annotation { "Feature Type Name" : "Feature", "Feature Type Description" : "" }
export const myFeature = defineFeature(function(context is Context, id is Id, definition is map)
    precondition{}
    {
        {
            var Q0;
            Q0=qCreatedBy(makeId("Top.planeOp"),FACE);
            var sketch = newSketch(context, id + "F0", { "sketchPlane" : qUnion([Q0])});
            skLineSegment(sketch, "E0.bottom", {"start": v(-19.05, 12.7) * mm, "end": v(19.05, 12.7) * mm});
            skLineSegment(sketch, "E0.top", {"start": v(-25.4, -25.4) * mm, "end": v(25.4, -25.4) * mm});
            skLineSegment(sketch, "E0.left", {"start": v(-25.4, 6.35) * mm, "end": v(-25.4, -25.4) * mm});
            skLineSegment(sketch, "E0.right", {"start": v(25.4, 6.35) * mm, "end": v(25.4, -25.4) * mm});
            skLineSegment(sketch, "E1.0", {"start": v(-17.78, 11.43) * mm, "end": v(17.78, 11.43) * mm});
            skLineSegment(sketch, "E1.1", {"start": v(-24.13, 5.08) * mm, "end": v(-24.13, -22.86) * mm});
            skLineSegment(sketch, "E1.2", {"start": v(-22.86, -24.13) * mm, "end": v(22.86, -24.13) * mm});
            skLineSegment(sketch, "E1.3", {"start": v(24.13, 5.08) * mm, "end": v(24.13, -22.86) * mm});
            skLineSegment(sketch, "E2.top", {"start": v(-25.4, -38.1) * mm, "end": v(25.4, -38.1) * mm});
            skLineSegment(sketch, "E2.left", {"start": v(-25.4, -27.94) * mm, "end": v(-25.4, -38.1) * mm});
            skLineSegment(sketch, "E2.right", {"start": v(25.4, -27.94) * mm, "end": v(25.4, -38.1) * mm});
            skLineSegment(sketch, "E3", {"start": v(-25.4, -27.94) * mm, "end": v(25.4, -27.94) * mm});
            skPoint(sketch, "E3.endSnap0", {"position": v(25.4, -31.75) * mm});
            skLineSegment(sketch, "E4", {"start": v(-20.32, -25.4) * mm, "end": v(-20.32, -27.94) * mm});
            skLineSegment(sketch, "E5", {"start": v(20.32, -25.4) * mm, "end": v(20.32, -27.94) * mm});
            skPoint(sketch, "E6.visualSharp", {"position": v(-24.13, 11.43) * mm});
            skArc(sketch, "E6.filletArc", {"start": v(-17.78, 11.43) * mm, "mid": v(-22.27, 9.57) * mm, "end": v(-24.13, 5.08) * mm});
            skPoint(sketch, "E7.visualSharp", {"position": v(-25.4, 12.7) * mm});
            skArc(sketch, "E7.filletArc", {"start": v(-19.05, 12.7) * mm, "mid": v(-23.54, 10.84) * mm, "end": v(-25.4, 6.35) * mm});
            skPoint(sketch, "E8.visualSharp", {"position": v(24.13, 11.43) * mm});
            skArc(sketch, "E8.filletArc", {"start": v(24.13, 5.08) * mm, "mid": v(22.27, 9.57) * mm, "end": v(17.78, 11.43) * mm});
            skPoint(sketch, "E9.visualSharp", {"position": v(25.4, 12.7) * mm});
            skArc(sketch, "E9.filletArc", {"start": v(25.4, 6.35) * mm, "mid": v(23.54, 10.84) * mm, "end": v(19.05, 12.7) * mm});
            skArc(sketch, "E10.filletArc", {"start": v(-24.13, -22.86) * mm, "mid": v(-23.76, -23.76) * mm, "end": v(-22.86, -24.13) * mm});
            skArc(sketch, "E11.filletArc", {"start": v(22.86, -24.13) * mm, "mid": v(23.76, -23.76) * mm, "end": v(24.13, -22.86) * mm});
            skSolve(sketch);
        }
        {
            var Q0;
            Q0=makeQuery(id+"F0.imprint","IMPRINT",FACE,{"disambiguationData":[TD([[makeQuery(id+"F0.imprint","IMPRINT",EDGE,{"derivedFrom":sQuery(id+"F0.wireOp",EDGE,"E0.bottom")}),-1.0]])]});
            extrude(context, id + "F1", {"entities" : qUnion([Q0]), "depth" : 50.8 * mm});
        }
        {
            var Q0;
            Q0=makeQuery(id+"F0.imprint","IMPRINT",FACE,{"disambiguationData":[TD([[makeQuery(id+"F0.imprint","IMPRINT",EDGE,{"derivedFrom":sQuery(id+"F0.wireOp",EDGE,"E1.0")}),-1.0]])]});
            var Q1;
            {var subQ0=sQuery(id+"F0.wireOp",EDGE,"E4");Q1=makeQuery(id+"F0.imprint","IMPRINT",FACE,{"disambiguationData":[TD([[makeQuery(id+"F0.imprint","IMPRINT",EDGE,{"derivedFrom":subQ0}),1.0]])]});}
            extrude(context, id + "F2", {"entities" : qUnion([Q0, Q1]), "operationType" : NewBodyOperationType.ADD, "depth" : 0.5 * mm});
        }
        {
            var Q0;
            Q0=makeQuery(id+"F0.imprint","IMPRINT",FACE,{"disambiguationData":[TD([[makeQuery(id+"F0.imprint","IMPRINT",EDGE,{"derivedFrom":sQuery(id+"F0.wireOp",EDGE,"E2.top")}),1.0]])]});
            extrude(context, id + "F3", {"entities" : qUnion([Q0]), "operationType" : NewBodyOperationType.ADD, "depth" : 7.62 * mm});
        }
        {
            var Q0;
            Q0=makeQuery(id+"F3.opExtrude","CAP_EDGE",EDGE,{"disambiguationData":[OSD([sQuery(id+"F0.wireOp",EDGE,"E2.top")])],"isStart":false});
            chamfer(context, id + "F4", {"entities" : qUnion([Q0]), "chamferType" : ChamferType.TWO_OFFSETS, "width1" : 8.9 * mm, "oppositeDirection" : false, "width2" : 3.8 * mm, "tangentPropagation" : true});
        }
        {
            var Q0;
            Q0=makeQuery(id+"F4.opChamfer","BLEND_FACE",FACE,{"disambiguationData":[OSD([sQuery(id+"F0.wireOp",EDGE,"E2.top")])]});
            var Q1;
            Q1=makeQuery(id+"F3.opExtrude","SWEPT_EDGE",EDGE,{"disambiguationData":[OSD([sQuery(id+"F0.wireOp",EDGE,"E2.left"),sQuery(id+"F0.wireOp",EDGE,"E3")])]});
            var Q2;
            Q2=makeQuery(id+"F3.opExtrude","SWEPT_EDGE",EDGE,{"disambiguationData":[OSD([sQuery(id+"F0.wireOp",EDGE,"E2.top"),sQuery(id+"F0.wireOp",EDGE,"E2.left")])]});
            var Q3;
            Q3=makeQuery(id+"F3.opExtrude","SWEPT_EDGE",EDGE,{"disambiguationData":[OSD([sQuery(id+"F0.wireOp",EDGE,"E2.top"),sQuery(id+"F0.wireOp",EDGE,"E2.right")])]});
            var Q4;
            Q4=makeQuery(id+"F3.opExtrude","SWEPT_EDGE",EDGE,{"disambiguationData":[OSD([sQuery(id+"F0.wireOp",EDGE,"E2.right"),sQuery(id+"F0.wireOp",EDGE,"E3")])]});
            fillet(context, id + "F5", {"entities" : qUnion([Q0, Q1, Q2, Q3, Q4]), "radius" : 1.27 * mm, "tangentPropagation" : true, "allowEdgeOverflow" : false});
        }
        {
            var Q0;
            Q0=makeQuery(id+"F1.opExtrude","SWEPT_FACE",FACE,{"disambiguationData":[OSD([sQuery(id+"F0.wireOp",EDGE,"E0.top")])]});
            var sketch = newSketch(context, id + "F6", { "sketchPlane" : qUnion([Q0])});
            skLineSegment(sketch, "E12.bottom", {"start": v(-15.24, 47) * mm, "end": v(15.24, 47) * mm});
            skLineSegment(sketch, "E12.top", {"start": v(-15.24, 11.43) * mm, "end": v(15.24, 11.43) * mm});
            skLineSegment(sketch, "E12.left", {"start": v(-21.59, 40.64) * mm, "end": v(-21.59, 17.78) * mm});
            skLineSegment(sketch, "E12.right", {"start": v(21.6, 40.64) * mm, "end": v(21.6, 17.78) * mm});
            skPoint(sketch, "E13.visualSharp", {"position": v(-21.59, 47) * mm});
            skArc(sketch, "E13.filletArc", {"start": v(-15.24, 47) * mm, "mid": v(-19.73, 45.13) * mm, "end": v(-21.59, 40.64) * mm});
            skPoint(sketch, "E14.visualSharp", {"position": v(-21.6, 11.43) * mm});
            skArc(sketch, "E14.filletArc", {"start": v(-21.59, 17.78) * mm, "mid": v(-19.73, 13.29) * mm, "end": v(-15.24, 11.43) * mm});
            skPoint(sketch, "E15.visualSharp", {"position": v(21.6, 11.43) * mm});
            skArc(sketch, "E15.filletArc", {"start": v(15.24, 11.43) * mm, "mid": v(19.73, 13.29) * mm, "end": v(21.6, 17.78) * mm});
            skPoint(sketch, "E16.visualSharp", {"position": v(21.6, 47) * mm});
            skArc(sketch, "E16.filletArc", {"start": v(21.6, 40.64) * mm, "mid": v(19.73, 45.13) * mm, "end": v(15.24, 46.99) * mm});
            skSolve(sketch);
        }
        {
            var Q0;
            Q0=makeQuery(id+"F6.imprint","IMPRINT",FACE,{"disambiguationData":[TD([[makeQuery(id+"F6.imprint","IMPRINT",EDGE,{"derivedFrom":sQuery(id+"F6.wireOp",EDGE,"E12.bottom")}),-1.0]])]});
            extrude(context, id + "F7", {"entities" : qUnion([Q0]), "operationType" : NewBodyOperationType.REMOVE, "oppositeDirection" : true, "depth" : 0.38 * mm});
        }
        {
            var Q0;
            Q0=makeQuery(id+"F7.boolean.opBoolean","COPY",FACE,{"derivedFrom":makeQuery(id+"F7.opExtrude","CAP_FACE",FACE,{"disambiguationData":[OSD([sQuery(id+"F6.wireOp",EDGE,"E12.bottom"),sQuery(id+"F6.wireOp",EDGE,"E12.top"),sQuery(id+"F6.wireOp",EDGE,"E12.left"),sQuery(id+"F6.wireOp",EDGE,"E12.right"),sQuery(id+"F6.wireOp",EDGE,"E13.filletArc"),sQuery(id+"F6.wireOp",EDGE,"E14.filletArc"),sQuery(id+"F6.wireOp",EDGE,"E15.filletArc"),sQuery(id+"F6.wireOp",EDGE,"E16.filletArc")])],"isStart":false})});
            var sketch = newSketch(context, id + "F8", { "sketchPlane" : qUnion([Q0])});
            skText(sketch, "E17", { "text": "DA DA", "fontName": "OpenSans-Regular.ttf"});
            skPoint(sketch, "E17.firstSnap0", {"position": v(-19.73, 45.13) * mm});
            const initialGuessF8  = {"E17": [-0.01973, 0.02564, 1, 0, 0.0093]};
            skSetInitialGuess(sketch, initialGuessF8);
            skSolve(sketch);
        }
        {
            var Q0;
            Q0 = qSketchRegion(id + "F8", true);
            extrude(context, id + "F9", {"entities" : qUnion([Q0]), "operationType" : NewBodyOperationType.ADD, "depth" : 0.38 * mm});
        }
        {
            var Q0;
            Q0=makeQuery(id+"F1.opExtrude","SWEPT_FACE",FACE,{"disambiguationData":[OSD([sQuery(id+"F0.wireOp",EDGE,"E0.right")])]});
            var sketch = newSketch(context, id + "F10", { "sketchPlane" : qUnion([Q0])});
            skLineSegment(sketch, "E18.bottom", {"start": v(-25.4, 31.75) * mm, "end": v(6.35, 31.75) * mm});
            skLineSegment(sketch, "E18.top", {"start": v(-25.4, 25.4) * mm, "end": v(6.35, 25.4) * mm});
            skLineSegment(sketch, "E18.left", {"start": v(-25.4, 31.75) * mm, "end": v(-25.4, 25.4) * mm});
            skLineSegment(sketch, "E18.right", {"start": v(6.35, 31.75) * mm, "end": v(6.35, 25.4) * mm});
            skSolve(sketch);
        }
        {
            var Q0;
            Q0=makeQuery(id+"F10.imprint","IMPRINT",FACE,{"disambiguationData":[TD([[makeQuery(id+"F10.imprint","IMPRINT",EDGE,{"derivedFrom":sQuery(id+"F10.wireOp",EDGE,"E18.bottom")}),-1.0]])]});
            extrude(context, id + "F11", {"entities" : qUnion([Q0]), "operationType" : NewBodyOperationType.REMOVE, "oppositeDirection" : true, "depth" : 0.25 * mm});
        }
        {
            var Q0;
            Q0=makeQuery(id+"F1.opExtrude","SWEPT_FACE",FACE,{"disambiguationData":[OSD([sQuery(id+"F0.wireOp",EDGE,"E0.left")])]});
            var sketch = newSketch(context, id + "F12", { "sketchPlane" : qUnion([Q0])});
            skLineSegment(sketch, "E19.bottom", {"start": v(25.4, 31.75) * mm, "end": v(-6.35, 31.75) * mm});
            skLineSegment(sketch, "E19.top", {"start": v(25.4, 25.4) * mm, "end": v(-6.35, 25.4) * mm});
            skLineSegment(sketch, "E19.left", {"start": v(25.4, 31.75) * mm, "end": v(25.4, 25.4) * mm});
            skLineSegment(sketch, "E19.right", {"start": v(-6.35, 31.75) * mm, "end": v(-6.35, 25.4) * mm});
            skSolve(sketch);
        }
        {
            var Q0;
            Q0=makeQuery(id+"F12.imprint","IMPRINT",FACE,{"disambiguationData":[TD([[makeQuery(id+"F12.imprint","IMPRINT",EDGE,{"derivedFrom":sQuery(id+"F12.wireOp",EDGE,"E19.bottom")}),1.0]])]});
            extrude(context, id + "F13", {"entities" : qUnion([Q0]), "operationType" : NewBodyOperationType.REMOVE, "oppositeDirection" : true, "depth" : 0.25 * mm});
        }
        {
            var Q0;
            Q0=makeQuery(id+"F9.opExtrude","CAP_EDGE",EDGE,{"disambiguationData":[OSD([sQuery(id+"F8.wireOp",EDGE,"E17.sketch_text.stroke-2")])],"isStart":true});
            var Q1;
            Q1=makeQuery(id+"F9.opExtrude","CAP_EDGE",EDGE,{"disambiguationData":[OSD([sQuery(id+"F8.wireOp",EDGE,"E17.sketch_text.stroke-17")])],"isStart":true});
            var Q2;
            Q2=makeQuery(id+"F9.opExtrude","CAP_EDGE",EDGE,{"disambiguationData":[OSD([sQuery(id+"F8.wireOp",EDGE,"E17.sketch_text.stroke-18")])],"isStart":true});
            var Q3;
            Q3=makeQuery(id+"F9.opExtrude","CAP_EDGE",EDGE,{"disambiguationData":[OSD([sQuery(id+"F8.wireOp",EDGE,"E17.sketch_text.stroke-15")])],"isStart":true});
            var Q4;
            Q4=makeQuery(id+"F9.opExtrude","CAP_EDGE",EDGE,{"disambiguationData":[OSD([sQuery(id+"F8.wireOp",EDGE,"E17.sketch_text.stroke-21")])],"isStart":true});
            var Q5;
            Q5=makeQuery(id+"F9.boolean.opBoolean","SPLIT",FACE,{"disambiguationData":[TD([makeQuery(id+"F9.opExtrude","SWEPT_FACE",FACE,{"disambiguationData":[OSD([sQuery(id+"F8.wireOp",EDGE,"E17.sketch_text.stroke-49")])]})])],"derivedFrom":makeQuery(id+"F7.boolean.opBoolean","COPY",FACE,{"derivedFrom":makeQuery(id+"F7.opExtrude","CAP_FACE",FACE,{"disambiguationData":[OSD([sQuery(id+"F6.wireOp",EDGE,"E12.bottom"),sQuery(id+"F6.wireOp",EDGE,"E12.top"),sQuery(id+"F6.wireOp",EDGE,"E12.left"),sQuery(id+"F6.wireOp",EDGE,"E12.right"),sQuery(id+"F6.wireOp",EDGE,"E13.filletArc"),sQuery(id+"F6.wireOp",EDGE,"E14.filletArc"),sQuery(id+"F6.wireOp",EDGE,"E15.filletArc"),sQuery(id+"F6.wireOp",EDGE,"E16.filletArc")])],"isStart":false})})});
            var Q6;
            Q6=makeQuery(id+"F9.boolean.opBoolean","SPLIT",FACE,{"disambiguationData":[TD([makeQuery(id+"F9.opExtrude","SWEPT_FACE",FACE,{"disambiguationData":[OSD([sQuery(id+"F8.wireOp",EDGE,"E17.sketch_text.stroke-34")])]})])],"derivedFrom":makeQuery(id+"F7.boolean.opBoolean","COPY",FACE,{"derivedFrom":makeQuery(id+"F7.opExtrude","CAP_FACE",FACE,{"disambiguationData":[OSD([sQuery(id+"F6.wireOp",EDGE,"E12.bottom"),sQuery(id+"F6.wireOp",EDGE,"E12.top"),sQuery(id+"F6.wireOp",EDGE,"E12.left"),sQuery(id+"F6.wireOp",EDGE,"E12.right"),sQuery(id+"F6.wireOp",EDGE,"E13.filletArc"),sQuery(id+"F6.wireOp",EDGE,"E14.filletArc"),sQuery(id+"F6.wireOp",EDGE,"E15.filletArc"),sQuery(id+"F6.wireOp",EDGE,"E16.filletArc")])],"isStart":false})})});
            var Q7;
            Q7=makeQuery(id+"F9.opExtrude","CAP_EDGE",EDGE,{"disambiguationData":[OSD([sQuery(id+"F8.wireOp",EDGE,"E17.sketch_text.stroke-30")])],"isStart":true});
            var Q8;
            Q8=makeQuery(id+"F9.opExtrude","CAP_EDGE",EDGE,{"disambiguationData":[OSD([sQuery(id+"F8.wireOp",EDGE,"E17.sketch_text.stroke-42")])],"isStart":true});
            var Q9;
            Q9=makeQuery(id+"F9.opExtrude","CAP_EDGE",EDGE,{"disambiguationData":[OSD([sQuery(id+"F8.wireOp",EDGE,"E17.sketch_text.stroke-28")])],"isStart":true});
            var Q10;
            Q10=makeQuery(id+"F9.opExtrude","CAP_EDGE",EDGE,{"disambiguationData":[OSD([sQuery(id+"F8.wireOp",EDGE,"E17.sketch_text.stroke-43")])],"isStart":true});
            var Q11;
            Q11=makeQuery(id+"F9.opExtrude","CAP_EDGE",EDGE,{"disambiguationData":[OSD([sQuery(id+"F8.wireOp",EDGE,"E17.sketch_text.stroke-48")])],"isStart":true});
            var Q12;
            Q12=makeQuery(id+"F9.opExtrude","CAP_EDGE",EDGE,{"disambiguationData":[OSD([sQuery(id+"F8.wireOp",EDGE,"E17.sketch_text.stroke-44")])],"isStart":true});
            var Q13;
            {var subQ0=sQuery(id+"F6.wireOp",EDGE,"E12.right");var subQ1=sQuery(id+"F6.wireOp",EDGE,"E16.filletArc");var subQ2=sQuery(id+"F6.wireOp",EDGE,"E12.top");var subQ3=sQuery(id+"F6.wireOp",EDGE,"E12.left");var subQ4=sQuery(id+"F6.wireOp",EDGE,"E12.bottom");var subQ5=sQuery(id+"F6.wireOp",EDGE,"E13.filletArc");var subQ6=sQuery(id+"F6.wireOp",EDGE,"E14.filletArc");var subQ7=sQuery(id+"F6.wireOp",EDGE,"E15.filletArc");Q13=makeQuery(id+"F9.boolean.opBoolean","SPLIT",FACE,{"disambiguationData":[TD([makeQuery(id+"F7.boolean.opBoolean","COPY",FACE,{"derivedFrom":makeQuery(id+"F7.opExtrude","SWEPT_FACE",FACE,{"disambiguationData":[OSD([subQ4])]})})])],"derivedFrom":makeQuery(id+"F7.boolean.opBoolean","COPY",FACE,{"derivedFrom":makeQuery(id+"F7.opExtrude","CAP_FACE",FACE,{"disambiguationData":[OSD([subQ4,subQ2,subQ3,subQ0,subQ5,subQ6,subQ7,subQ1])],"isStart":false})})});}
            chamfer(context, id + "F14", {"entities" : qUnion([Q0, Q1, Q2, Q3, Q4, Q5, Q6, Q7, Q8, Q9, Q10, Q11, Q12, Q13]), "width" : 0.25 * mm, "tangentPropagation" : true});
        }
    });